FCSTD DOCUMENT  (FreeCAD 0.20R29177 +426 (Git))
Label: imageRecogAssembly
License: All rights reserved
LicenseURL: http://en.wikipedia.org/wiki/All_rights_reserved
objects: App::Link×6, App::DocumentObjectGroup×4, PartDesign::CoordinateSystem×1, App::FeaturePython×1, App::Part×1
note: 1 computed .brp shape members not serialized (recipe doc carries the construction recipe); baked Part::Feature solids carry a one-line shape summary decoded from their .brp
EXTERNAL_REF file=ImageRecogBox.FCStd obj=LCS_2
EXTERNAL_REF file=ImageRecogBox.FCStd obj=Body
EXTERNAL_REF file=ImageRecogBox.FCStd obj=LCS_1
EXTERNAL_REF file=MG90S_servo_refined.FCStd obj=LCS_1
EXTERNAL_REF file=MG90S_servo_refined.FCStd obj=Body
EXTERNAL_REF file=MG90S_servo_refined.FCStd obj=LCS_2
EXTERNAL_REF file=PortalRotatorSketch.FCStd obj=LCS_Origin
EXTERNAL_REF file=PortalRotatorSketch.FCStd obj=PortalRotatorBody
EXTERNAL_REF file=PortalRotatorSketch.FCStd obj=LCSRotator
EXTERNAL_REF file=refinedHorn.FCStd obj=LCS_1
EXTERNAL_REF file=refinedHorn.FCStd obj=Body
EXTERNAL_REF file=hornHexagonModified.FCStd obj=hexagonPlacement
EXTERNAL_REF file=refinedHorn.FCStd obj=hexagonPlacement_LCS
EXTERNAL_REF file=hornHexagonModified.FCStd obj=Body
EXTERNAL_REF file=ImageRecogBox.FCStd obj=LCS_cam
EXTERNAL_REF file=esp32camMountRefined.FCStd obj=LCS_1
EXTERNAL_REF file=esp32camMountRefined.FCStd obj=Body

FEATURE [App::DocumentObjectGroup] Parts
FEATURE [PartDesign::CoordinateSystem] LCS_Origin
  AttacherType = Attacher::AttachEngine3D
  MapMode = 2
  Support = -> [X_Axis]
FEATURE [App::DocumentObjectGroup] Constraints
FEATURE [App::FeaturePython] Variables  # WARN: FeaturePython — macro-defined, semantics opaque (R4)
  PortalRotatorDeg = -143
  Type = App::PropertyContainer
FEATURE [App::DocumentObjectGroup] Configurations
FEATURE [App::Link] ImageRecogBox_body  label="ImageRecogBox-body"
  AttachedBy = #LCS_2
  AttachedTo = Parent Assembly#LCS_Origin
  LinkedObject = -> <external ImageRecogBox.FCStd>#Body
  SolverId = Asm4EE
  expr: Placement = LCS_Origin.Placement * AttachmentOffset * ImageRecogBox#LCS_2.Placement ^ -1
FEATURE [App::Link] Body
  AttachedBy = #LCS_1
  AttachedTo = ImageRecogBox_body#LCS_1
  AttachmentOffset = pos=(0,0,0) rot=(0.57735,0.57735,0.57735;2.0944rad)
  LinkPlacement = pos=(-1514.39,-470.078,-777.809) rot=(0.57735,0.57735,0.57735;2.0944rad)
  LinkedObject = -> <external MG90S_servo_refined.FCStd>#Body
  Placement = pos=(-1514.39,-470.078,-777.809) rot=(0.57735,0.57735,0.57735;2.0944rad)
  SolverId = Asm4EE
  expr: Placement = ImageRecogBox_body.Placement * ImageRecogBox#LCS_1.Placement * AttachmentOffset * MG90S_servo_refined#LCS_1.Placement ^ -1
FEATURE [App::Link] PortalRotatorBody
  AttachedBy = #LCS_Origin
  AttachedTo = Body#LCS_2
  AttachmentOffset = pos=(0,0,0) rot=(0,0,1;1.5708rad)
  LinkPlacement = pos=(82.6025,-25.2832,-10.6) rot=(0,0,1;3.14159rad)
  LinkedObject = -> <external PortalRotatorSketch.FCStd>#PortalRotatorBody
  Placement = pos=(82.6025,-25.2832,-10.6) rot=(0,0,1;3.14159rad)
  SolverId = Asm4EE
  expr: Placement = Body.Placement * MG90S_servo_refined#LCS_2.Placement * AttachmentOffset * PortalRotatorSketch#LCS_Origin.Placement ^ -1
FEATURE [App::Link] HornBody
  AttachedBy = #LCS_1
  AttachedTo = PortalRotatorBody#LCSRotator
  AttachmentOffset = pos=(0,0,0) rot=(1,0,0;4.71239rad)
  LinkPlacement = pos=(232.111,275.116,-8.90904) rot=(-0.34483,-0.938665,0;3.14159rad)
  LinkedObject = -> <external refinedHorn.FCStd>#Body
  Placement = pos=(232.111,275.116,-8.90904) rot=(-0.34483,-0.938665,0;3.14159rad)
  SolverId = Asm4EE
  expr: Placement = PortalRotatorBody.Placement * PortalRotatorSketch#LCSRotator.Placement * AttachmentOffset * refinedHorn#LCS_1.Placement ^ -1
FEATURE [App::Link] hornHexagonBody
  AttachedBy = #hexagonPlacement
  AttachedTo = HornBody#hexagonPlacement_LCS
  LinkPlacement = pos=(129.828,-98.4677,-11.911) rot=(0,0,-1;3.86029rad)
  LinkedObject = -> <external hornHexagonModified.FCStd>#Body
  Placement = pos=(129.828,-98.4677,-11.911) rot=(0,0,-1;3.86029rad)
  SolverId = Asm4EE
  expr: Placement = HornBody.Placement * refinedHorn#hexagonPlacement_LCS.Placement * AttachmentOffset * hornHexagonModified#hexagonPlacement.Placement ^ -1
FEATURE [App::DocumentObjectGroup] Measures
FEATURE [App::Link] mountBody
  AttachedBy = #LCS_1
  AttachedTo = ImageRecogBox_body#LCS_cam
  LinkPlacement = pos=(51.135,-80.5684,98.5891) rot=(0.023347,-0.087132,-0.995923;2.62003rad)
  LinkedObject = -> <external esp32camMountRefined.FCStd>#Body
  Placement = pos=(51.135,-80.5684,98.5891) rot=(0.023347,-0.087132,-0.995923;2.62003rad)
  SolverId = Asm4EE
  expr: Placement = ImageRecogBox_body.Placement * ImageRecogBox#LCS_cam.Placement * AttachmentOffset * esp32camMountRefined#LCS_1.Placement ^ -1
FEATURE [App::Part] Assembly
  AssemblyType = Part::Link
  Group = -> [LCS_Origin,Constraints,Variables,Configurations,ImageRecogBox_body,Body,PortalRotatorBody,HornBody,hornHexagonBody,mountBody]
  Origin = -> Origin
  Type = Assembly

RESOLVED EXTERNAL PARTS (link-assembly join: the EXTERNAL_REF files above that resolve inside this repo's crawl, each included once):
---- part ImageRecogBox.FCStd = doc fcstd_bc312f18e636 ----
FCSTD DOCUMENT  (FreeCAD 0.20R29177 +426 (Git))
Label: ImageRecogBox
License: All rights reserved
LicenseURL: http://en.wikipedia.org/wiki/All_rights_reserved
objects: Sketcher::SketchObject×17, PartDesign::Pad×12, PartDesign::CoordinateSystem×5, PartDesign::Chamfer×4, PartDesign::Pocket×3, PartDesign::Hole×2, PartDesign::Body×1
note: 65 computed .brp shape members not serialized (recipe doc carries the construction recipe); baked Part::Feature solids carry a one-line shape summary decoded from their .brp

FEATURE [Sketcher::SketchObject] Sketch
  FullyConstrained = true
  MapMode = 5
  Support = -> [XY_Plane]
  sketch-geometry (14):
    g0: LineSegment StartX=86.6025 StartY=50 StartZ=0 EndX=0 EndY=100 EndZ=0
    g1: LineSegment StartX=4.3e-15 StartY=100 StartZ=0 EndX=-86.6025 EndY=50 EndZ=0
    g2: LineSegment StartX=-86.6025 StartY=50 StartZ=0 EndX=-86.6025 EndY=-50 EndZ=0
    g3: LineSegment StartX=-86.6025 StartY=-50 StartZ=0 EndX=0 EndY=-100 EndZ=0
    g4: LineSegment StartX=0 StartY=-100 StartZ=0 EndX=86.6025 EndY=-50 EndZ=0
    g5: LineSegment StartX=86.6025 StartY=-50 StartZ=0 EndX=86.6025 EndY=50 EndZ=0
    g6: Circle CenterX=0 CenterY=0 CenterZ=0 NormalX=0 NormalY=0 NormalZ=1 AngleXU=0 Radius=100
    g7: LineSegment StartX=87.4686 StartY=-50.5 StartZ=0 EndX=87.4686 EndY=50.5 EndZ=0
    g8: LineSegment StartX=87.4686 StartY=50.5 StartZ=0 EndX=-1.42e-14 EndY=101 EndZ=0
    g9: LineSegment StartX=-1.48e-14 StartY=101 StartZ=0 EndX=-87.4686 EndY=50.5 EndZ=0
    g10: LineSegment StartX=-87.4686 StartY=50.5 StartZ=0 EndX=-87.4686 EndY=-50.5 EndZ=0
    g11: LineSegment StartX=-87.4686 StartY=-50.5 StartZ=0 EndX=0 EndY=-101 EndZ=0
    g12: LineSegment StartX=0 StartY=-101 StartZ=0 EndX=87.4686 EndY=-50.5 EndZ=0
    g13: Circle CenterX=0 CenterY=0 CenterZ=0 NormalX=0 NormalY=0 NormalZ=1 AngleXU=0 Radius=101
  constraints (33):
    c: Coincident(g0,g1)
    c: Coincident(g1,g2)
    c: Coincident(g2,g3)
    c: Coincident(g3,g4)
    c: Coincident(g4,g5)
    c: Coincident(g5,g0)
    c: Equal(g0, g1-g5) x5
    c: PointOnObject(g0,g6)
    c: PointOnObject(g1,g6)
    c: PointOnObject(g2,g6)
    c: PointOnObject(g3,g6)
    c: PointOnObject(g4,g6)
    c: PointOnObject(g5,g6)
    c: Coincident(g6,g-1)
    c: Vertical(g5)
    c: Coincident(g7,g8)
    c: Coincident(g8,g9)
    c: Coincident(g9,g10)
    c: Coincident(g10,g11)
    c: Coincident(g11,g12)
    c: Coincident(g12,g7)
    c: Equal(g7, g8-g12) x5
    c: PointOnObject(g7,g13)
    c: PointOnObject(g8,g13)
    c: PointOnObject(g9,g13)
    c: PointOnObject(g10,g13)
    c: PointOnObject(g11,g13)
    c: PointOnObject(g12,g13)
    c: Coincident(g13,g6)
    c: Vertical(g7)
    c: Diameter(g6) = 200
    c: DistanceY(g5,g5) = 100
    c: Diameter(g13) = 202
FEATURE [PartDesign::Pad] Pad
  Direction = (0,0,1)
  Length = 150
  Length2 = 10
  Profile = -> Sketch
  ReferenceAxis = -> Sketch [N_Axis]
  Type = 0
FEATURE [Sketcher::SketchObject] Sketch001
  ExternalGeometry = -> [Pad]
  FullyConstrained = true
  MapMode = 5
  Placement = pos=(0,0,0) rot=(1,0,0;3.14159rad)
  Support = -> [Pad]
  sketch-geometry (4):
    g0: LineSegment StartX=103.603 StartY=0 StartZ=0 EndX=86.6025 EndY=0 EndZ=0
    g1: LineSegment StartX=86.6025 StartY=0 StartZ=0 EndX=86.6025 EndY=-10 EndZ=0
    g2: LineSegment StartX=86.6025 StartY=-10 StartZ=0 EndX=103.603 EndY=-10 EndZ=0
    g3: LineSegment StartX=103.603 StartY=-10 StartZ=0 EndX=103.603 EndY=0 EndZ=0
  constraints (12):
    c: Coincident(g0,g1)
    c: Coincident(g1,g2)
    c: Coincident(g2,g3)
    c: Coincident(g3,g0)
    c: Horizontal(g0)
    c: Horizontal(g2)
    c: Vertical(g1)
    c: Vertical(g3)
    c: PointOnObject(g1,g-3)
    c: DistanceX(g2,g2) = 17
    c: DistanceY(g3,g3) = 10
    c: PointOnObject(g0,g-1)
FEATURE [PartDesign::Pad] Pad001
  BaseFeature = -> Pad
  Direction = (0,0,-1)
  Length = 25
  Length2 = 10
  Profile = -> Sketch001
  ReferenceAxis = -> Sketch001 [N_Axis]
  Type = 0
FEATURE [Sketcher::SketchObject] Sketch002
  ExternalGeometry = -> [Pad001]
  FullyConstrained = true
  MapMode = 5
  Placement = pos=(0,0,-25) rot=(1,0,0;3.14159rad)
  Support = -> [Pad001]
  sketch-geometry (4):
    g0: LineSegment StartX=103.603 StartY=-10 StartZ=0 EndX=73.6025 EndY=-10 EndZ=0
    g1: LineSegment StartX=73.6025 StartY=-10 StartZ=0 EndX=73.6025 EndY=50 EndZ=0
    g2: LineSegment StartX=73.6025 StartY=50 StartZ=0 EndX=103.603 EndY=50 EndZ=0
    g3: LineSegment StartX=103.603 StartY=50 StartZ=0 EndX=103.603 EndY=-10 EndZ=0
  constraints (11):
    c: Coincident(g0,g1)
    c: Coincident(g2,g3)
    c: Coincident(g3,g0)
    c: Horizontal(g0)
    c: Vertical(g3)
    c: Coincident(g0,g-4)
    c: Coincident(g2,g1)
    c: Horizontal(g2)
    c: Horizontal(g2,g-6)
    c: Vertical(g1)
    c: DistanceX(g0,g0) = 30
FEATURE [PartDesign::Pad] Pad002
  BaseFeature = -> Pad001
  Direction = (0,0,-1)
  Length = 8
  Length2 = 10
  Profile = -> Sketch002
  ReferenceAxis = -> Sketch002 [N_Axis]
  Type = 0
FEATURE [Sketcher::SketchObject] Sketch003
  ExternalGeometry = -> [Pad002]
  FullyConstrained = true
  MapMode = 5
  Placement = pos=(0,0,-25) rot=(0,0,1;0rad)
  Support = -> [Pad002]
  sketch-geometry (6):
    g0: LineSegment StartX=76.1025 StartY=-8 StartZ=0 EndX=89.1025 EndY=-8 EndZ=0
    g1: LineSegment StartX=89.1025 StartY=-8 StartZ=0 EndX=89.1025 EndY=-32 EndZ=0
    g2: LineSegment StartX=89.1025 StartY=-32 StartZ=0 EndX=76.1025 EndY=-32 EndZ=0
    g3: LineSegment StartX=76.1025 StartY=-32 StartZ=0 EndX=76.1025 EndY=-8 EndZ=0
    g4: GeomPoint X=82.6025 Y=-20 Z=0
    g5: GeomPoint X=88.6025 Y=-20 Z=0
  constraints (14):
    c: Coincident(g0,g1)
    c: Coincident(g1,g2)
    c: Coincident(g2,g3)
    c: Coincident(g3,g0)
    c: Horizontal(g0)
    c: Horizontal(g2)
    c: Vertical(g1)
    c: Vertical(g3)
    c: DistanceY(g1,g1) = 24
    c: DistanceX(g2,g2) = 13
    c: Symmetric(g1,g0,g4)
    c: Symmetric(g-5,g-3,g5)
    c: DistanceX(g4,g5) = 6
    c: Horizontal(g5,g4)
FEATURE [PartDesign::Pocket] Pocket
  BaseFeature = -> Pad002
  Direction = (0,0,-1)
  Length = 19
  Length2 = 5
  Profile = -> Sketch003
  ReferenceAxis = -> Sketch003 [N_Axis]
  Type = 1
FEATURE [Sketcher::SketchObject] Sketch004
  ExternalGeometry = -> [Pocket]
  FullyConstrained = false
  MapMode = 5
  Placement = pos=(0,0,-25) rot=(0,0,1;0rad)
  Support = -> [Pocket]
  sketch-geometry (5):
    g0: GeomPoint X=82.6025 Y=-6.3796 Z=0
    g1: GeomPoint X=82.6025 Y=-33.3796 Z=0
    g2: Circle CenterX=82.6025 CenterY=-6.3796 CenterZ=0 NormalX=0 NormalY=0 NormalZ=1 AngleXU=0 Radius=1
    g3: Circle CenterX=82.6025 CenterY=-33.3796 CenterZ=0 NormalX=0 NormalY=0 NormalZ=1 AngleXU=0 Radius=1
    g4: GeomPoint X=82.6025 Y=-20 Z=0
  constraints (8):
    c: DistanceY(g1,g0) = 27
    c: Coincident(g2,g0)
    c: Coincident(g3,g1)
    c: Equal(g3,g2)
    c: Diameter(g2) = 2
    c: Symmetric(g-6,g-5,g4)
    c: Vertical(g2,g3)
    c: Vertical(g3,g4)
FEATURE [PartDesign::Hole] Hole
  BaseFeature = -> Pocket
  CustomThreadClearance = 0
  Depth = 25
  DepthType = 0
  Diameter = 1.6
  DrillForDepth = false
  DrillPoint = 1
  DrillPointAngle = 118
  HoleCutCountersinkAngle = 90
  HoleCutCustomValues = false
  HoleCutDepth = 0
  HoleCutDiameter = 6.1
  HoleCutType = 0
  ModelThread = false
  Profile = -> Sketch004
  Tapered = false
  TaperedAngle = 90
  ThreadClass = 0
  ThreadDepth = 25
  ThreadDepthType = 0
  ThreadDirection = 0
  ThreadFit = 0
  ThreadSize = 6
  ThreadType = 1
  Threaded = true
  UseCustomThreadClearance = false
FEATURE [PartDesign::CoordinateSystem] LCS_1
  AttacherType = Attacher::AttachEngine3D
  MapMode = 45
  Placement = pos=(82.6025,-6.3796,-25) rot=(0,0,1;0rad)
  Support = -> [Hole]
FEATURE [PartDesign::CoordinateSystem] LCS_2  label="LCS_origin"
  AttacherType = Attacher::AttachEngine3D
FEATURE [PartDesign::Chamfer] Chamfer
  Angle = 45
  Base = -> Hole [Edge4]
  BaseFeature = -> Hole
  ChamferType = 0
  FlipDirection = false
  Size = 16
  Size2 = 1
  SupportTransform = false
  UseAllEdges = false
FEATURE [PartDesign::Chamfer] Chamfer001
  Angle = 45
  Base = -> Chamfer [Edge12,Edge49]
  BaseFeature = -> Chamfer
  ChamferType = 0
  FlipDirection = false
  Size = 3
  Size2 = 1
  SupportTransform = false
  UseAllEdges = false
FEATURE [Sketcher::SketchObject] Sketch005
  ExternalGeometry = -> [Chamfer001]
  FullyConstrained = true
  MapMode = 5
  Placement = pos=(0,0,0) rot=(1,0,0;3.14159rad)
  Support = -> [Chamfer001]
  sketch-geometry (8):
    g0: LineSegment StartX=86.6025 StartY=-10 StartZ=0 EndX=86.6025 EndY=-50 EndZ=0
    g1: LineSegment StartX=86.6025 StartY=-50 StartZ=0 EndX=0 EndY=-100 EndZ=0
    g2: LineSegment StartX=0 StartY=-100 StartZ=0 EndX=-86.6025 EndY=-50 EndZ=0
    g3: LineSegment StartX=-86.6025 StartY=-50 StartZ=0 EndX=-87.4686 EndY=-50.5 EndZ=0
    g4: LineSegment StartX=-87.4686 StartY=-50.5 StartZ=0 EndX=-1.42e-14 EndY=-101 EndZ=0
    g5: LineSegment StartX=-1.42e-14 StartY=-101 StartZ=0 EndX=87.4686 EndY=-50.5 EndZ=0
    g6: LineSegment StartX=87.4686 StartY=-50.5 StartZ=0 EndX=87.4686 EndY=-10 EndZ=0
    g7: LineSegment StartX=87.4686 StartY=-10 StartZ=0 EndX=86.6025 EndY=-10 EndZ=0
  constraints (16):
    c: Coincident(g-7,g0)
    c: Coincident(g0,g-7)
    c: Coincident(g0,g1)
    c: Coincident(g1,g-4)
    c: Coincident(g1,g2)
    c: Coincident(g2,g-3)
    c: Coincident(g2,g3)
    c: Coincident(g3,g-5)
    c: Coincident(g3,g4)
    c: Coincident(g4,g-6)
    c: Coincident(g4,g5)
    c: Coincident(g5,g-8)
    c: Coincident(g5,g6)
    c: Coincident(g6,g-8)
    c: Coincident(g6,g7)
    c: Coincident(g7,g0)
FEATURE [PartDesign::Pad] Pad003
  BaseFeature = -> Chamfer001
  Direction = (0,0,-1)
  Length = 12
  Length2 = 10
  Profile = -> Sketch005
  ReferenceAxis = -> Sketch005 [N_Axis]
  Type = 0
FEATURE [Sketcher::SketchObject] Sketch006
  ExternalGeometry = -> [Pad003]
  FullyConstrained = true
  MapMode = 5
  Placement = pos=(0,0,-12) rot=(1,0,0;3.14159rad)
  Support = -> [Pad003]
  sketch-geometry (17):
    g0: LineSegment StartX=87.4686 StartY=-10 StartZ=0 EndX=77.4686 EndY=-10 EndZ=0
    g1: LineSegment StartX=77.4686 StartY=-44.7265 StartZ=0 EndX=77.4686 EndY=-10 EndZ=0
    g2: LineSegment StartX=-77.4686 StartY=44.7265 StartZ=0 EndX=-77.4686 EndY=-44.7265 EndZ=0
    g3: LineSegment StartX=-77.4686 StartY=-44.7265 StartZ=0 EndX=1.42e-14 EndY=-89.453 EndZ=0
    g4: LineSegment StartX=1.42e-14 StartY=-89.453 StartZ=0 EndX=77.4686 EndY=-44.7265 EndZ=0
    g5: Circle CenterX=0 CenterY=0 CenterZ=0 NormalX=0 NormalY=0 NormalZ=1 AngleXU=0 Radius=89.453
    g6: LineSegment StartX=87.4686 StartY=-10 StartZ=0 EndX=87.4686 EndY=-50.5 EndZ=0
    g7: LineSegment StartX=87.4686 StartY=-50.5 StartZ=0 EndX=0 EndY=-101 EndZ=0
    g8: LineSegment StartX=0 StartY=-101 StartZ=0 EndX=-87.4686 EndY=-50.5 EndZ=0
    g9: LineSegment StartX=-87.4686 StartY=-50.5 StartZ=0 EndX=-87.4686 EndY=50.5 EndZ=0
    g10: LineSegment StartX=-87.4686 StartY=50.5 StartZ=0 EndX=1.42e-14 EndY=101 EndZ=0
    g11: LineSegment StartX=1.42e-14 StartY=101 StartZ=0 EndX=90 EndY=101 EndZ=0
    g12: LineSegment StartX=90 StartY=101 StartZ=0 EndX=172.942 EndY=53.1132 EndZ=0
    g13: LineSegment StartX=-77.4686 StartY=44.7265 StartZ=0 EndX=0 EndY=89.453 EndZ=0
    g14: LineSegment StartX=0 StartY=89.453 StartZ=0 EndX=90 EndY=89.453 EndZ=0
    g15: LineSegment StartX=90 StartY=89.453 StartZ=0 EndX=167.942 EndY=44.453 EndZ=0
    g16: LineSegment StartX=172.942 StartY=53.1132 StartZ=0 EndX=167.942 EndY=44.453 EndZ=0
  constraints (44):
    c: Coincident(g-3,g0)
    c: Horizontal(g0)
    c: DistanceX(g0,g0) = 10
    c: Coincident(g2,g3)
    c: Coincident(g3,g4)
    c: Coincident(g4,g1)
    c: PointOnObject(g2,g5)
    c: PointOnObject(g2,g5)
    c: PointOnObject(g3,g5)
    c: PointOnObject(g4,g5)
    c: Coincident(g5,g-1)
    c: Vertical(g1)
    c: Coincident(g6,g0)
    c: Coincident(g6,g-4)
    c: Coincident(g7,g6)
    c: Coincident(g7,g-5)
    c: Coincident(g8,g7)
    c: Coincident(g8,g-6)
    c: Coincident(g9,g8)
    c: Coincident(g9,g-6)
    c: Coincident(g1,g0)
    c: Parallel(g-8,g4)
    c: Parallel(g3,g-9)
    c: Vertical(g2)
    c: DistanceX(g8,g2) = 10
    c: Coincident(g10,g9)
    c: Coincident(g10,g-11)
    c: Coincident(g11,g10)
    c: Horizontal(g11)
    c: Coincident(g12,g11)
    c: Parallel(g12,g3)
    c: Coincident(g13,g2)
    c: PointOnObject(g13,g5)
    c: Parallel(g13,g10)
    c: Coincident(g14,g13)
    c: Horizontal(g14)
    c: Vertical(g14,g11)
    c: DistanceX(g14,g14) = 90
    c: Coincident(g15,g14)
    c: Coincident(g16,g12)
    c: Coincident(g16,g15)
    c: Parallel(g15,g12)
    c: Perpendicular(g12,g16)
    c: Distance(g15) = 90
FEATURE [PartDesign::Pad] Pad004
  BaseFeature = -> Pad003
  Direction = (0,0,-1)
  Length = 5
  Length2 = 10
  Profile = -> Sketch006
  ReferenceAxis = -> Sketch006 [N_Axis]
  Type = 0
FEATURE [Sketcher::SketchObject] Sketch007
  ExternalGeometry = -> [Pad004]
  FullyConstrained = true
  MapMode = 5
  Placement = pos=(43.7343,-75.75,0) rot=(0.935113,0.250563,0.250563;1.63783rad)
  Support = -> [Pad004]
  sketch-geometry (5):
    g0: LineSegment StartX=-30 StartY=130 StartZ=0 EndX=30 EndY=130 EndZ=0
    g1: LineSegment StartX=30 StartY=130 StartZ=0 EndX=30 EndY=60 EndZ=0
    g2: LineSegment StartX=30 StartY=60 StartZ=0 EndX=-30 EndY=60 EndZ=0
    g3: LineSegment StartX=-30 StartY=60 StartZ=0 EndX=-30 EndY=130 EndZ=0
    g4: GeomPoint X=0 Y=130 Z=0
  constraints (13):
    c: Coincident(g0,g1)
    c: Coincident(g1,g2)
    c: Coincident(g2,g3)
    c: Coincident(g3,g0)
    c: Horizontal(g0)
    c: Horizontal(g2)
    c: Vertical(g1)
    c: Vertical(g3)
    c: PointOnObject(g4,g-2)
    c: Symmetric(g0,g0,g4)
    c: DistanceX(g0,g0) = 60
    c: DistanceY(g0,g-3) = 20
    c: DistanceY(g1,g1) = 70
FEATURE [PartDesign::Pad] Pad005
  BaseFeature = -> Pad004
  Direction = (0.5,-0.866025,0)
  Length = 30
  Length2 = 10
  Profile = -> Sketch007
  ReferenceAxis = -> Sketch007 [N_Axis]
  Type = 0
FEATURE [Sketcher::SketchObject] Sketch008
  ExternalGeometry = -> [Pad005]
  FullyConstrained = true
  MapMode = 5
  Placement = pos=(43.3013,-75,0) rot=(-0.186157,0.694747,0.694747;3.50969rad)
  Support = -> [Pad005]
  sketch-geometry (4):
    g0: LineSegment StartX=-25 StartY=58 StartZ=0 EndX=25 EndY=58 EndZ=0
    g1: LineSegment StartX=25 StartY=58 StartZ=0 EndX=25 EndY=132 EndZ=0
    g2: LineSegment StartX=25 StartY=132 StartZ=0 EndX=-25 EndY=132 EndZ=0
    g3: LineSegment StartX=-25 StartY=132 StartZ=0 EndX=-25 EndY=58 EndZ=0
  constraints (12):
    c: Coincident(g0,g1)
    c: Coincident(g1,g2)
    c: Coincident(g2,g3)
    c: Coincident(g3,g0)
    c: Horizontal(g0)
    c: Horizontal(g2)
    c: Vertical(g1)
    c: Vertical(g3)
    c: DistanceY(g-4,g1) = 2
    c: DistanceX(g1,g-4) = 5
    c: DistanceX(g-5,g2) = 5
    c: DistanceY(g0,g-6) = 2
FEATURE [PartDesign::Pocket] Pocket001
  BaseFeature = -> Pad005
  Direction = (0.5,-0.866025,-1e-16)
  Length = 5
  Length2 = 5
  Profile = -> Sketch008
  ReferenceAxis = -> Sketch008 [N_Axis]
  Type = 1
FEATURE [Sketcher::SketchObject] Sketch009
  ExternalGeometry = -> [Pocket001]
  FullyConstrained = true
  MapMode = 5
  Placement = pos=(25.9808,15,0) rot=(0.377964,0.654654,0.654654;2.41886rad)
  Support = -> [Pocket001]
  sketch-geometry (2):
    g0: Circle CenterX=-102.469 CenterY=110 CenterZ=0 NormalX=0 NormalY=0 NormalZ=1 AngleXU=0 Radius=3
    g1: GeomPoint X=-102.469 Y=130 Z=0
  constraints (4):
    c: Diameter(g0) = 6
    c: Symmetric(g-3,g-4,g1)
    c: Vertical(g1,g0)
    c: DistanceY(g0,g1) = 20
FEATURE [PartDesign::Hole] Hole001
  BaseFeature = -> Pocket001
  CustomThreadClearance = 0
  Depth = 25
  DepthType = 0
  Diameter = 2.5
  DrillForDepth = false
  DrillPoint = 1
  DrillPointAngle = 118
  HoleCutCountersinkAngle = 90
  HoleCutCustomValues = false
  HoleCutDepth = 0
  HoleCutDiameter = 6.1
  HoleCutType = 2
  ModelThread = false
  Profile = -> Sketch009
  Tapered = false
  TaperedAngle = 90
  ThreadClass = 0
  ThreadDepth = 25
  ThreadDepthType = 0
  ThreadDirection = 0
  ThreadFit = 0
  ThreadSize = 9
  ThreadType = 1
  Threaded = true
  UseCustomThreadClearance = false
FEATURE [PartDesign::CoordinateSystem] LCS_cam
  AttacherType = Attacher::AttachEngine3D
  AttachmentOffset = pos=(0,0,0) rot=(-0.766044,-0.642788,0;3.14159rad)
  MapMode = 45
  Placement = pos=(72.8849,-76.2404,110) rot=(0.754536,-0.528332,-0.389282;1.75037rad)
  Support = -> [Hole001]
FEATURE [Sketcher::SketchObject] Sketch010
  FullyConstrained = true
  MapMode = 5
  Placement = pos=(-43.7343,75.75,0) rot=(-0.186157,0.694747,0.694747;3.50969rad)
  Support = -> [Hole001]
  sketch-geometry (5):
    g0: LineSegment StartX=10 StartY=56 StartZ=0 EndX=10 EndY=36 EndZ=0
    g1: LineSegment StartX=10 StartY=36 StartZ=0 EndX=-10 EndY=36 EndZ=0
    g2: LineSegment StartX=-10 StartY=36 StartZ=0 EndX=-10 EndY=56 EndZ=0
    g3: LineSegment StartX=-10 StartY=56 StartZ=0 EndX=10 EndY=56 EndZ=0
    g4: GeomPoint X=0 Y=46 Z=0
  constraints (13):
    c: Coincident(g0,g1)
    c: Coincident(g1,g2)
    c: Coincident(g2,g3)
    c: Coincident(g3,g0)
    c: Horizontal(g1)
    c: Horizontal(g3)
    c: Vertical(g0)
    c: Vertical(g2)
    c: Symmetric(g1,g0,g4)
    c: PointOnObject(g4,g-2)
    c: DistanceX(g1,g1) = 20
    c: DistanceY(g0,g0) = 20
    c: DistanceY(g-1,g0) = 36
FEATURE [PartDesign::Pad] Pad006
  BaseFeature = -> Hole001
  Direction = (-0.5,0.866025,1e-16)
  Length = 90
  Length2 = 10
  Profile = -> Sketch010
  ReferenceAxis = -> Sketch010 [N_Axis]
  Type = 0
FEATURE [Sketcher::SketchObject] Sketch011
  ExternalGeometry = -> [Pad006]
  FullyConstrained = true
  MapMode = 5
  Placement = pos=(2.2e-15,-3.6e-15,36) rot=(1,0,0;3.14159rad)
  Support = -> [Pad006]
  sketch-geometry (4):
    g0: LineSegment StartX=-97.3945 StartY=-148.692 StartZ=0 EndX=-87.3945 EndY=-131.372 EndZ=0
    g1: LineSegment StartX=-87.3945 StartY=-131.372 StartZ=0 EndX=-70.074 EndY=-141.372 EndZ=0
    g2: LineSegment StartX=-70.074 StartY=-141.372 StartZ=0 EndX=-80.074 EndY=-158.692 EndZ=0
    g3: LineSegment StartX=-80.074 StartY=-158.692 StartZ=0 EndX=-97.3945 EndY=-148.692 EndZ=0
  constraints (10):
    c: Coincident(g-5,g0)
    c: PointOnObject(g0,g-4)
    c: Coincident(g0,g1)
    c: PointOnObject(g1,g-3)
    c: Coincident(g1,g2)
    c: Coincident(g2,g-5)
    c: Coincident(g2,g3)
    c: Coincident(g3,g0)
    c: Perpendicular(g2,g1)
    c: Equal(g2,g3)
FEATURE [PartDesign::Pad] Pad007
  BaseFeature = -> Pad006
  Direction = (-1e-16,1e-16,-1)
  Length = 40
  Length2 = 10
  Profile = -> Sketch011
  ReferenceAxis = -> Sketch011 [N_Axis]
  Type = 0
FEATURE [Sketcher::SketchObject] Sketch012
  ExternalGeometry = -> [Pad007]
  FullyConstrained = true
  MapMode = 5
  Placement = pos=(-7e-16,1.2e-15,-4) rot=(1,0,0;3.14159rad)
  Support = -> [Pad007]
  sketch-geometry (1):
    g0: Circle CenterX=-83.7343 CenterY=-145.032 CenterZ=0 NormalX=0 NormalY=0 NormalZ=1 AngleXU=0 Radius=3
  constraints (2):
    c: Diameter(g0) = 6
    c: Symmetric(g-5,g-6,g0)
FEATURE [PartDesign::Pocket] Pocket002
  BaseFeature = -> Pad007
  Direction = (2e-16,-3e-16,1)
  Length = 20
  Length2 = 5
  Profile = -> Sketch012
  ReferenceAxis = -> Sketch012 [N_Axis]
  Type = 0
FEATURE [PartDesign::Chamfer] Chamfer002
  Angle = 45
  Base = -> Pocket002 [Edge200,Edge207,Edge209,Edge205]
  BaseFeature = -> Pocket002
  ChamferType = 0
  FlipDirection = false
  Size = 4
  Size2 = 1
  SupportTransform = false
  UseAllEdges = false
FEATURE [PartDesign::CoordinateSystem] LCS_forRod
  AttacherType = Attacher::AttachEngine3D
  AttachmentOffset = pos=(0,0,0) rot=(0,0,1;0.523599rad)
  MapMode = 45
  Placement = pos=(-83.7343,145.032,16) rot=(0,0,1;0.523648rad)
  Support = -> [Chamfer002]
FEATURE [Sketcher::SketchObject] Sketch013
  FullyConstrained = true
  MapMode = 5
  Placement = pos=(-43.7343,-75.75,0) rot=(0.935113,-0.250563,-0.250563;1.63783rad)
  Support = -> [Chamfer002]
  sketch-geometry (5):
    g0: LineSegment StartX=10 StartY=46 StartZ=0 EndX=10 EndY=26 EndZ=0
    g1: LineSegment StartX=10 StartY=26 StartZ=0 EndX=-10 EndY=26 EndZ=0
    g2: LineSegment StartX=-10 StartY=26 StartZ=0 EndX=-10 EndY=46 EndZ=0
    g3: LineSegment StartX=-10 StartY=46 StartZ=0 EndX=10 EndY=46 EndZ=0
    g4: GeomPoint X=0 Y=36 Z=0
  constraints (13):
    c: Coincident(g0,g1)
    c: Coincident(g1,g2)
    c: Coincident(g2,g3)
    c: Coincident(g3,g0)
    c: Horizontal(g1)
    c: Horizontal(g3)
    c: Vertical(g0)
    c: Vertical(g2)
    c: Symmetric(g1,g0,g4)
    c: PointOnObject(g4,g-2)
    c: DistanceY(g0,g0) = 20
    c: Equal(g3,g0)
    c: DistanceY(g-1,g4) = 36
FEATURE [PartDesign::Pad] Pad008
  BaseFeature = -> Chamfer002
  Direction = (-0.5,-0.866025,-1e-16)
  Length = 200
  Length2 = 10
  Profile = -> Sketch013
  ReferenceAxis = -> Sketch013 [N_Axis]
  Type = 0
FEATURE [Sketcher::SketchObject] Sketch014
  ExternalGeometry = -> [Pad008]
  FullyConstrained = true
  MapMode = 5
  Placement = pos=(-1.6e-15,-2.6e-15,26) rot=(1,0,0;3.14159rad)
  Support = -> [Pad008]
  sketch-geometry (4):
    g0: LineSegment StartX=-152.395 StartY=243.955 StartZ=0 EndX=-135.074 EndY=253.955 EndZ=0
    g1: LineSegment StartX=-135.074 StartY=253.955 StartZ=0 EndX=-125.074 EndY=236.635 EndZ=0
    g2: LineSegment StartX=-125.074 StartY=236.635 StartZ=0 EndX=-142.395 EndY=226.635 EndZ=0
    g3: LineSegment StartX=-142.395 StartY=226.635 StartZ=0 EndX=-152.395 EndY=243.955 EndZ=0
  constraints (10):
    c: Coincident(g-4,g0)
    c: Coincident(g0,g-5)
    c: Coincident(g0,g1)
    c: PointOnObject(g1,g-5)
    c: Coincident(g1,g2)
    c: PointOnObject(g2,g-4)
    c: Coincident(g2,g3)
    c: Coincident(g3,g0)
    c: Perpendicular(g1,g2)
    c: Equal(g1,g0)
FEATURE [PartDesign::Pad] Pad009
  BaseFeature = -> Pad008
  Direction = (1e-16,1e-16,-1)
  Length = 430
  Length2 = 10
  Profile = -> Sketch014
  ReferenceAxis = -> Sketch014 [N_Axis]
  Type = 0
FEATURE [Sketcher::SketchObject] Sketch015
  FullyConstrained = true
  MapMode = 5
  Placement = pos=(87.4686,0,0) rot=(0.57735,0.57735,0.57735;2.0944rad)
  Support = -> [Pad009]
  sketch-geometry (5):
    g0: LineSegment StartX=-10 StartY=46 StartZ=0 EndX=-10 EndY=26 EndZ=0
    g1: LineSegment StartX=-10 StartY=26 StartZ=0 EndX=10 EndY=26 EndZ=0
    g2: LineSegment StartX=10 StartY=26 StartZ=0 EndX=10 EndY=46 EndZ=0
    g3: LineSegment StartX=10 StartY=46 StartZ=0 EndX=-10 EndY=46 EndZ=0
    g4: GeomPoint X=0 Y=36 Z=0
  constraints (13):
    c: Coincident(g0,g1)
    c: Coincident(g1,g2)
    c: Coincident(g2,g3)
    c: Coincident(g3,g0)
    c: Horizontal(g1)
    c: Horizontal(g3)
    c: Vertical(g0)
    c: Vertical(g2)
    c: Symmetric(g1,g0,g4)
    c: PointOnObject(g4,g-2)
    c: DistanceY(g2,g2) = 20
    c: Equal(g3,g2)
    c: DistanceY(g-1,g4) = 36
FEATURE [PartDesign::Pad] Pad010
  BaseFeature = -> Pad009
  Direction = (1,0,0)
  Length = 200
  Length2 = 10
  Profile = -> Sketch015
  ReferenceAxis = -> Sketch015 [N_Axis]
  Type = 0
FEATURE [Sketcher::SketchObject] Sketch016
  ExternalGeometry = -> [Pad010]
  FullyConstrained = true
  MapMode = 5
  Placement = pos=(0,0,26) rot=(1,0,0;3.14159rad)
  Support = -> [Pad010]
  sketch-geometry (4):
    g0: LineSegment StartX=287.469 StartY=10 StartZ=0 EndX=287.469 EndY=-10 EndZ=0
    g1: LineSegment StartX=287.469 StartY=-10 StartZ=0 EndX=267.469 EndY=-10 EndZ=0
    g2: LineSegment StartX=267.469 StartY=-10 StartZ=0 EndX=267.469 EndY=10 EndZ=0
    g3: LineSegment StartX=267.469 StartY=10 StartZ=0 EndX=287.469 EndY=10 EndZ=0
  constraints (10):
    c: Coincident(g-4,g0)
    c: Coincident(g0,g-5)
    c: Coincident(g0,g1)
    c: PointOnObject(g1,g-5)
    c: Coincident(g1,g2)
    c: PointOnObject(g2,g-4)
    c: Vertical(g2)
    c: Coincident(g2,g3)
    c: Coincident(g3,g0)
    c: Equal(g0,g3)
FEATURE [PartDesign::Pad] Pad011
  BaseFeature = -> Pad010
  Direction = (0,0,-1)
  Length = 430
  Length2 = 10
  Profile = -> Sketch016
  ReferenceAxis = -> Sketch016 [N_Axis]
  Type = 0
FEATURE [PartDesign::Chamfer] Chamfer003
  Angle = 45
  Base = -> Pad011 [Edge134,Edge132,Edge133,Edge138,Edge226,Edge137,Edge141,Edge231,Edge183,Edge176,Edge181,Edge244,Edge179,Edge184,Edge250]
  BaseFeature = -> Pad011
  ChamferType = 0
  FlipDirection = false
  Size = 3
  Size2 = 1
  SupportTransform = false
  UseAllEdges = false
FEATURE [PartDesign::CoordinateSystem] LCS_fall
  AttacherType = Attacher::AttachEngine3D
  AttachmentOffset = pos=(67,600,0) rot=(0,0,1;0rad)
  MapMode = 45
  Placement = pos=(9.80127,-16.9763,600) rot=(0.377964,0.654654,0.654654;2.41886rad)
  Support = -> [Chamfer003]
FEATURE [PartDesign::Body] Body  label="ImageRecogBox-body"
  Group = -> [Sketch,Pad,Sketch001,Pad001,Sketch002,Pad002,Sketch003,Pocket,Sketch004,Hole,LCS_1,LCS_2,Chamfer,Chamfer001,Sketch005,Pad003,Sketch006,Pad004,Sketch007,Pad005,Sketch008,Pocket001,Sketch009,Hole001,LCS_cam,Sketch010,Pad006,Sketch011,Pad007,Sketch012,Pocket002,Chamfer002,LCS_forRod,Sketch013,Pad008,Sketch014,Pad009,Sketch015,Pad010,Sketch016,Pad011,Chamfer003,LCS_fall]
  Origin = -> Origin
  Tip = -> Chamfer003
---- part MG90S_servo_refined.FCStd = doc fcstd_32f2eeedc879 ----
FCSTD DOCUMENT  (FreeCAD 0.20R29177 +426 (Git))
Label: MG90S_servo_refined
License: All rights reserved
LicenseURL: http://en.wikipedia.org/wiki/All_rights_reserved
objects: App::MeasureDistance×9, PartDesign::CoordinateSystem×2, Mesh::Feature×1, Part::Feature×1, Part::Refine×1, PartDesign::FeatureBase×1, Sketcher::SketchObject×1, PartDesign::Body×1
note: 7 computed .brp shape members not serialized (recipe doc carries the construction recipe); baked Part::Feature solids carry a one-line shape summary decoded from their .brp

FEATURE [Mesh::Feature] ImageToStl_com_MG90S  label="ImageToStl.com_MG90S"
FEATURE [Part::Feature] ImageToStl_com_MG90S001
  shape: bbox 33 x 32.4 x 12.2 mm, 2058 faces, 0 solids (baked)
FEATURE [Part::Refine] ImageToStl_com_MG90S001001
  Source = -> ImageToStl_com_MG90S001
FEATURE [App::MeasureDistance] Distance  label="Distance: 4,98 mm"
  Distance = 4.981
  P1 = (466.695,752.809,1601.93)
  P2 = (461.739,752.809,1601.42)
FEATURE [App::MeasureDistance] Distance001  label="Distance: 2,10 mm"
  Distance = 2.10355
  P1 = (466.695,752.809,1597.49)
  P2 = (464.591,752.809,1597.49)
FEATURE [App::MeasureDistance] Distance002  label="Distance: 3,08 mm"
  Distance = 3.07833
  P1 = (466.695,752.809,1595.55)
  P2 = (463.617,752.809,1595.61)
FEATURE [App::MeasureDistance] Distance003  label="Distance: 17,99 mm"
  Distance = 17.9941
  P1 = (461.695,752.809,1603.09)
  P2 = (461.695,734.815,1603.09)
FEATURE [App::MeasureDistance] Distance004  label="Distance: 12,20 mm"
  Distance = 12.2
  P1 = (461.695,734.809,1603.09)
  P2 = (461.695,734.809,1590.89)
FEATURE [App::MeasureDistance] Distance005  label="Distance: 22,96 mm"
  Distance = 22.963
  P1 = (438.732,734.809,1590.94)
  P2 = (461.695,734.809,1590.89)
FEATURE [App::MeasureDistance] Distance006  label="Distance: 1,85 mm"
  Distance = 1.84541
  P1 = (461.786,752.809,1595.51)
  P2 = (463.631,752.809,1595.56)
FEATURE [App::MeasureDistance] Distance007  label="Distance: 1,97 mm"
  Distance = 1.96716
  P1 = (461.782,752.809,1594.87)
  P2 = (463.745,752.809,1594.75)
FEATURE [App::MeasureDistance] Distance008  label="Distance: 2,48 mm"
  Distance = 2.48096
  P1 = (462.797,755.29,1603.09)
  P2 = (462.745,752.809,1603.09)
FEATURE [PartDesign::FeatureBase] BaseFeature
  BaseFeature = -> ImageToStl_com_MG90S001001
FEATURE [PartDesign::CoordinateSystem] LCS_1
  AttacherType = Attacher::AttachEngine3D
  AttachmentOffset = pos=(1,0,0) rot=(0,0,1;0rad)
  MapMode = 45
  Placement = pos=(463.698,752.809,1596.99) rot=(0,0,1;0rad)
  Support = -> [BaseFeature]
FEATURE [PartDesign::CoordinateSystem] LCS_2
  AttacherType = Attacher::AttachEngine3D
  MapMode = 45
  Placement = pos=(444.795,767.209,1596.99) rot=(-1,0,0;1.5708rad)
  Support = -> [BaseFeature]
FEATURE [Sketcher::SketchObject] Sketch
  ExternalGeometry = -> [BaseFeature]
  FullyConstrained = false
  MapMode = 5
  Placement = pos=(0,752.809,0) rot=(1,0,0;1.5708rad)
  Support = -> [BaseFeature]
  sketch-geometry (3):
    g0: GeomPoint X=462.698 Y=1596.99 Z=0
    g1: GeomPoint X=463.698 Y=1596.99 Z=0
    g2: Circle CenterX=463.698 CenterY=1596.99 CenterZ=0 NormalX=0 NormalY=0 NormalZ=1 AngleXU=0 Radius=1.15
  constraints (3):
    c: Symmetric(g-3,g-3,g0)
    c: Coincident(g2,g1)
    c: Diameter(g2) = 2.3
FEATURE [PartDesign::Body] Body
  BaseFeature = -> ImageToStl_com_MG90S001001
  Group = -> [BaseFeature,LCS_1,LCS_2,Sketch]
  Origin = -> Origin
  Tip = -> BaseFeature
---- part PortalRotatorSketch.FCStd = doc fcstd_fcd322103c07 ----
FCSTD DOCUMENT  (FreeCAD 0.20R29177 +426 (Git))
Label: PortalRotatorSketch
License: All rights reserved
LicenseURL: http://en.wikipedia.org/wiki/All_rights_reserved
objects: PartDesign::CoordinateSystem×2, Sketcher::SketchObject×1, PartDesign::Body×1
note: 4 computed .brp shape members not serialized (recipe doc carries the construction recipe); baked Part::Feature solids carry a one-line shape summary decoded from their .brp
EXTERNAL_REF file=assembly4.FCStd obj=Variables

FEATURE [PartDesign::CoordinateSystem] LCS_Origin
  AttacherType = Attacher::AttachEngine3D
  MapMode = 2
  Support = -> [X_Axis]
FEATURE [Sketcher::SketchObject] Sketch
  FullyConstrained = true
  MapMode = 5
  Support = -> [XY_Plane]
  expr: Constraints[0] = assembly4#Variables.PortalRotatorDeg
  sketch-geometry (1):
    g0: LineSegment StartX=0 StartY=0 StartZ=0 EndX=6.8404 EndY=18.7939 EndZ=0
  constraints (3):
    c: Angle(g0,g-1) = -1.22173
    c: Coincident(g0,g-1)
    c: Distance(g0) = 20
FEATURE [PartDesign::CoordinateSystem] LCSRotator
  AttacherType = Attacher::AttachEngine3D
  MapMode = 7
  Placement = pos=(0,0,0) rot=(0.970288,-0.171088,-0.171088;1.60095rad)
  Support = -> [Sketch]
FEATURE [PartDesign::Body] PortalRotatorBody
  Group = -> [LCS_Origin,Sketch,LCSRotator]
  Origin = -> Origin
---- part esp32camMountRefined.FCStd = doc fcstd_4b9deea06e1b ----
FCSTD DOCUMENT  (FreeCAD 0.20R29177 +426 (Git))
Label: esp32camMountRefined
License: All rights reserved
LicenseURL: http://en.wikipedia.org/wiki/All_rights_reserved
objects: Part::Feature×2, Mesh::Feature×1, Part::Refine×1, PartDesign::FeatureBase×1, PartDesign::CoordinateSystem×1, PartDesign::Body×1
note: 6 computed .brp shape members not serialized (recipe doc carries the construction recipe); baked Part::Feature solids carry a one-line shape summary decoded from their .brp

FEATURE [Mesh::Feature] ImageToStl_com_esp_32_cam_mount  label="ImageToStl.com_esp+32+cam+mount"
  Placement = pos=(-52,-21,0) rot=(0,0,1;0rad)
FEATURE [Part::Feature] ImageToStl_com_esp_32_cam_mount001
  shape: bbox 40.3 x 20 x 20 mm, 552 faces, 0 solids (baked)
FEATURE [Part::Refine] ImageToStl_com_esp_32_cam_mount001001
  Source = -> ImageToStl_com_esp_32_cam_mount001
FEATURE [Part::Feature] ImageToStl_com_esp_32_cam_mount001001_solid  label="ImageToStl_com_esp_32_cam_mount001001 (Solid)"
  shape: bbox 40.3 x 20 x 20 mm, 137 faces (baked)
FEATURE [PartDesign::FeatureBase] BaseFeature
  BaseFeature = -> ImageToStl_com_esp_32_cam_mount001001_solid
FEATURE [PartDesign::CoordinateSystem] LCS_1
  AttacherType = Attacher::AttachEngine3D
  MapMode = 45
  Placement = pos=(-21,9,10) rot=(0.57735,0.57735,0.57735;2.0944rad)
  Support = -> [BaseFeature]
FEATURE [PartDesign::Body] Body  label="mountBody"
  BaseFeature = -> ImageToStl_com_esp_32_cam_mount001001_solid
  Group = -> [BaseFeature,LCS_1]
  Origin = -> Origin
  Tip = -> BaseFeature
---- part hornHexagonModified.FCStd = doc fcstd_71265372c9fc ----
FCSTD DOCUMENT  (FreeCAD 0.20R29177 +426 (Git))
Label: hornHexagonModified
License: All rights reserved
LicenseURL: http://en.wikipedia.org/wiki/All_rights_reserved
objects: Sketcher::SketchObject×3, PartDesign::Pad×1, PartDesign::Pocket×1, PartDesign::Hole×1, PartDesign::CoordinateSystem×1, PartDesign::Body×1
note: 11 computed .brp shape members not serialized (recipe doc carries the construction recipe); baked Part::Feature solids carry a one-line shape summary decoded from their .brp

FEATURE [Sketcher::SketchObject] Sketch
  FullyConstrained = true
  MapMode = 5
  Support = -> [XY_Plane]
  sketch-geometry (7):
    g0: LineSegment StartX=86.6025 StartY=-50 StartZ=0 EndX=86.6025 EndY=50 EndZ=0
    g1: LineSegment StartX=86.6025 StartY=50 StartZ=0 EndX=0 EndY=100 EndZ=0
    g2: LineSegment StartX=6e-15 StartY=100 StartZ=0 EndX=-86.6025 EndY=50 EndZ=0
    g3: LineSegment StartX=-86.6025 StartY=50 StartZ=0 EndX=-86.6025 EndY=-50 EndZ=0
    g4: LineSegment StartX=-86.6025 StartY=-50 StartZ=0 EndX=0 EndY=-100 EndZ=0
    g5: LineSegment StartX=0 StartY=-100 StartZ=0 EndX=86.6025 EndY=-50 EndZ=0
    g6: Circle CenterX=0 CenterY=0 CenterZ=0 NormalX=0 NormalY=0 NormalZ=1 AngleXU=0 Radius=100
  constraints (16):
    c: Coincident(g0,g1)
    c: Coincident(g1,g2)
    c: Coincident(g2,g3)
    c: Coincident(g3,g4)
    c: Coincident(g4,g5)
    c: Coincident(g5,g0)
    c: Equal(g0, g1-g5) x5
    c: PointOnObject(g0,g6)
    c: PointOnObject(g1,g6)
    c: PointOnObject(g2,g6)
    c: PointOnObject(g3,g6)
    c: PointOnObject(g4,g6)
    c: PointOnObject(g5,g6)
    c: Coincident(g6,g-1)
    c: Vertical(g0)
    c: Diameter(g6) = 200
FEATURE [PartDesign::Pad] Pad
  Direction = (0,0,1)
  Length = 5
  Length2 = 10
  Profile = -> Sketch
  ReferenceAxis = -> Sketch [N_Axis]
  Type = 0
FEATURE [Sketcher::SketchObject] Sketch003
  ExternalGeometry = -> [Pad]
  FullyConstrained = true
  MapMode = 5
  Placement = pos=(0,0,0) rot=(1,0,0;3.14159rad)
  Support = -> [Pad]
  sketch-geometry (5):
    g0: ArcOfCircle CenterX=82.4925 CenterY=24 CenterZ=0 NormalX=0 NormalY=0 NormalZ=1 AngleXU=0 Radius=3.24 StartAngle=4.6245 EndAngle=7.94187
    g1: ArcOfCircle CenterX=67.6825 CenterY=24 CenterZ=0 NormalX=0 NormalY=0 NormalZ=1 AngleXU=0 Radius=1.94 StartAngle=1.65869 EndAngle=4.6245
    g2: LineSegment StartX=67.5123 StartY=25.9325 StartZ=0 EndX=82.2081 EndY=27.2275 EndZ=0
    g3: LineSegment StartX=67.5123 StartY=22.0675 StartZ=0 EndX=82.2081 EndY=20.7725 EndZ=0
    g4: GeomPoint X=85.7325 Y=24 Z=0
  constraints (12):
    c: Diameter(g1) = 3.88
    c: Diameter(g0) = 6.48
    c: Tangent(g2,g0) = 1.5708
    c: Tangent(g2,g1) = 1.5708
    c: Tangent(g3,g1) = -1.5708
    c: Tangent(g3,g0) = -1.5708
    c: DistanceX(g1,g0) = 14.81
    c: Horizontal(g0,g1)
    c: PointOnObject(g4,g0)
    c: Horizontal(g4,g0)
    c: DistanceY(g4,g-3) = 26
    c: DistanceX(g4,g-3) = 0.87
FEATURE [PartDesign::Pocket] Pocket
  BaseFeature = -> Pad
  Direction = (0,0,1)
  Length = 3
  Length2 = 5
  Profile = -> Sketch003
  ReferenceAxis = -> Sketch003 [N_Axis]
  Type = 0
FEATURE [Sketcher::SketchObject] Sketch004
  ExternalGeometry = -> [Pocket]
  FullyConstrained = true
  MapMode = 5
  Placement = pos=(0,0,3) rot=(1,0,0;3.14159rad)
  Support = -> [Pocket]
  sketch-geometry (4):
    g0: Circle CenterX=67.2125 CenterY=24 CenterZ=0 NormalX=0 NormalY=0 NormalZ=1 AngleXU=0 Radius=0.5
    g1: GeomPoint X=65.7425 Y=24 Z=0
    g2: Circle CenterX=70.7825 CenterY=24 CenterZ=0 NormalX=0 NormalY=0 NormalZ=1 AngleXU=0 Radius=0.5
    g3: Circle CenterX=74.3525 CenterY=24 CenterZ=0 NormalX=0 NormalY=0 NormalZ=1 AngleXU=0 Radius=0.5
  constraints (11):
    c: Horizontal(g-3,g0)
    c: PointOnObject(g1,g-3)
    c: Horizontal(g-3,g1)
    c: DistanceX(g1,g0) = 1.47
    c: Horizontal(g2,g0)
    c: DistanceX(g0,g2) = 3.57
    c: Equal(g2,g0)
    c: Diameter(g2) = 1
    c: Diameter(g3) = 1
    c: Horizontal(g3,g2)
    c: DistanceX(g2,g3) = 3.57
FEATURE [PartDesign::Hole] Hole
  BaseFeature = -> Pocket
  CustomThreadClearance = 0
  Depth = 25
  DepthType = 0
  Diameter = 1.6
  DrillForDepth = false
  DrillPoint = 1
  DrillPointAngle = 118
  HoleCutCountersinkAngle = 90
  HoleCutCustomValues = false
  HoleCutDepth = 0
  HoleCutDiameter = 6.1
  HoleCutType = 0
  ModelThread = false
  Profile = -> Sketch004
  Tapered = false
  TaperedAngle = 90
  ThreadClass = 0
  ThreadDepth = 25
  ThreadDepthType = 0
  ThreadDirection = 0
  ThreadFit = 0
  ThreadSize = 6
  ThreadType = 1
  Threaded = true
  UseCustomThreadClearance = false
FEATURE [PartDesign::CoordinateSystem] hexagonPlacement
  AttacherType = Attacher::AttachEngine3D
  MapMode = 45
  Placement = pos=(76.9057,-24,3) rot=(0,0,1;1.5708rad)
  Support = -> [Hole]
FEATURE [PartDesign::Body] Body  label="hornHexagonBody"
  Group = -> [Sketch,Pad,Sketch003,Pocket,Sketch004,Hole,hexagonPlacement]
  Origin = -> Origin
  Tip = -> Hole
---- part refinedHorn.FCStd = doc fcstd_d6d8a35d817a ----
FCSTD DOCUMENT  (FreeCAD 0.20R29177 +426 (Git))
Label: refinedHorn
License: All rights reserved
LicenseURL: http://en.wikipedia.org/wiki/All_rights_reserved
objects: Part::Feature×2, PartDesign::CoordinateSystem×2, Mesh::Feature×1, Part::Refine×1, PartDesign::FeatureBase×1, Sketcher::SketchObject×1, PartDesign::Body×1
note: 8 computed .brp shape members not serialized (recipe doc carries the construction recipe); baked Part::Feature solids carry a one-line shape summary decoded from their .brp

FEATURE [Mesh::Feature] _0mm_servoHorn  label="20mm-servoHorn"
FEATURE [Part::Feature] _0mm_servoHorn001
  shape: bbox 20 x 6.479 x 6.445 mm, 2350 faces, 0 solids (baked)
FEATURE [Part::Refine] _0mm_servoHorn001001
  Source = -> _0mm_servoHorn001
FEATURE [Part::Feature] _0mm_servoHorn001001_solid  label="_0mm_servoHorn001001 (Solid)"
  shape: bbox 20 x 6.479 x 6.445 mm, 888 faces (baked)
FEATURE [PartDesign::FeatureBase] BaseFeature
  BaseFeature = -> _0mm_servoHorn001001_solid
FEATURE [PartDesign::CoordinateSystem] LCS_1
  AttacherType = Attacher::AttachEngine3D
  AttachmentOffset = pos=(0,0,0) rot=(0.382683,0.92388,0;3.14159rad)
  MapMode = 45
  Placement = pos=(-80.5131,-325.745,1.691) rot=(-0.686181,0.727431,0;3.14159rad)
  Support = -> [BaseFeature]
FEATURE [Sketcher::SketchObject] Sketch
  ExternalGeometry = -> [BaseFeature]
  FullyConstrained = true
  MapMode = 5
  Placement = pos=(0,0,0.002) rot=(1,0,0;3.14159rad)
  Support = -> [BaseFeature]
  sketch-geometry (5):
    g0: Circle CenterX=-95.4317 CenterY=325.96 CenterZ=0 NormalX=0 NormalY=0 NormalZ=1 AngleXU=0 Radius=1.94454
    g1: Circle CenterX=-80.6171 CenterY=325.74 CenterZ=0 NormalX=0 NormalY=0 NormalZ=1 AngleXU=0 Radius=3.24089
    g2: Circle CenterX=-95.9081 CenterY=325.959 CenterZ=0 NormalX=0 NormalY=0 NormalZ=1 AngleXU=0 Radius=0.435168
    g3: Circle CenterX=-92.3401 CenterY=325.959 CenterZ=0 NormalX=0 NormalY=0 NormalZ=1 AngleXU=0 Radius=0.435168
    g4: Circle CenterX=-88.7721 CenterY=325.959 CenterZ=0 NormalX=0 NormalY=0 NormalZ=1 AngleXU=0 Radius=0.435168
  constraints (21):
    c: PointOnObject(g-10,g0)
    c: PointOnObject(g-11,g0)
    c: PointOnObject(g-9,g0)
    c: PointOnObject(g-6,g1)
    c: PointOnObject(g-8,g1)
    c: PointOnObject(g-7,g1)
    c: Diameter(g1) = 6.48178
    c: Diameter(g0) = 3.88909
    c: DistanceX(g0,g1) = 14.8146
    c: PointOnObject(g-12,g2)
    c: PointOnObject(g-14,g2)
    c: PointOnObject(g-13,g2)
    c: PointOnObject(g-15,g3)
    c: PointOnObject(g-17,g3)
    c: PointOnObject(g-16,g3)
    c: DistanceX(g2,g3) = 3.568
    c: DistanceX(g-9,g2) = 1.46816
    c: PointOnObject(g-19,g4)
    c: PointOnObject(g-20,g4)
    c: PointOnObject(g-18,g4)
    c: DistanceX(g3,g4) = 3.568
FEATURE [PartDesign::CoordinateSystem] hexagonPlacement_LCS
  AttacherType = Attacher::AttachEngine3D
  AttachmentOffset = pos=(0,0,0) rot=(0,1,0;3.14159rad)
  MapMode = 45
  Placement = pos=(-87.3366,-325.835,0.002) rot=(-0.712245,0.701931,0;3.14159rad)
  Support = -> [BaseFeature]
FEATURE [PartDesign::Body] Body  label="HornBody"
  BaseFeature = -> _0mm_servoHorn001001_solid
  Group = -> [BaseFeature,LCS_1,Sketch,hexagonPlacement_LCS]
  Origin = -> Origin
  Tip = -> BaseFeature
